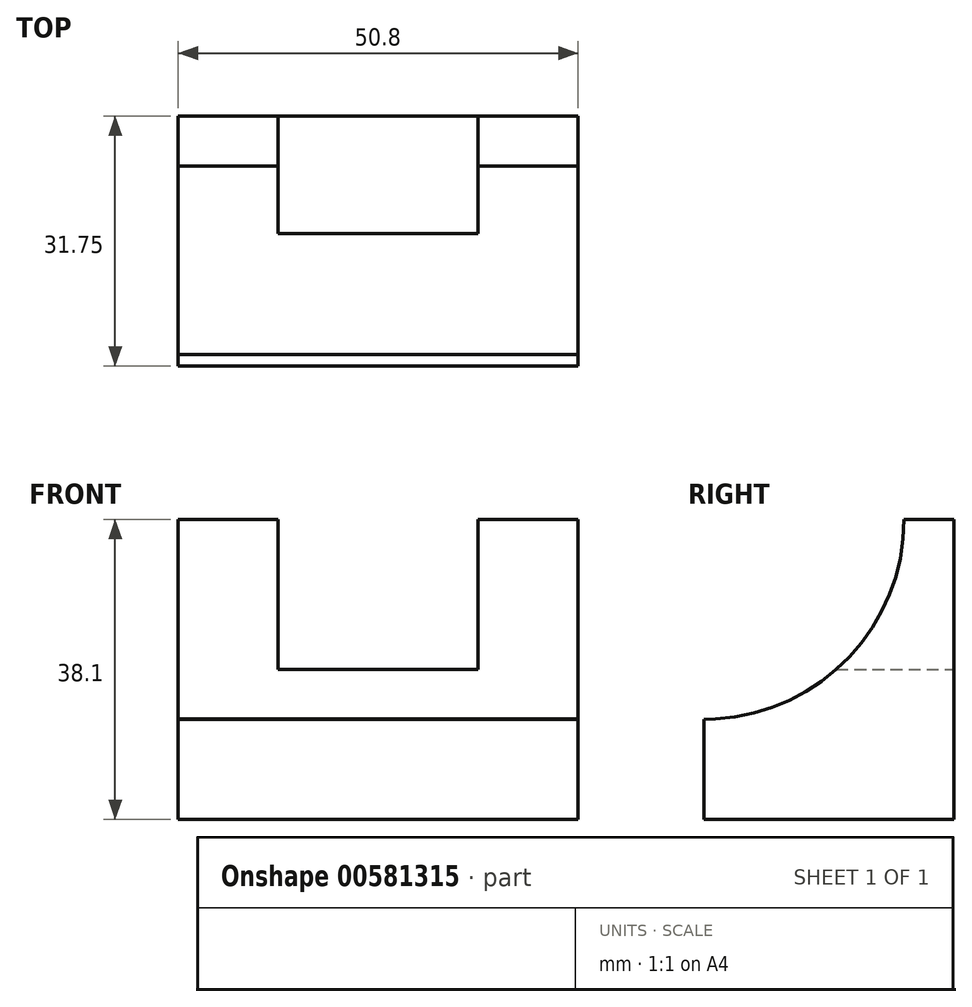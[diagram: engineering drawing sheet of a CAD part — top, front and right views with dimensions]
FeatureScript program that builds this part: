
annotation { "Feature Type Name" : "Feature", "Feature Type Description" : "" }
export const myFeature = defineFeature(function(context is Context, id is Id, definition is map)
    precondition{}
    {
        {
            var Q0;
            Q0=qCreatedBy(makeId("Front.planeOp"),FACE);
            var sketch = newSketch(context, id + "F0", { "sketchPlane" : qUnion([Q0])});
            skLineSegment(sketch, "E0.bottom", {"start": v(-10.98, 24.5) * mm, "end": v(39.82, 24.5) * mm});
            skLineSegment(sketch, "E0.top", {"start": v(-10.98, -13.6) * mm, "end": v(39.82, -13.6) * mm});
            skLineSegment(sketch, "E0.left", {"start": v(-10.98, 24.5) * mm, "end": v(-10.98, -13.6) * mm});
            skLineSegment(sketch, "E0.right", {"start": v(39.82, 24.5) * mm, "end": v(39.82, -13.6) * mm});
            skSolve(sketch);
        }
        {
            var Q0;
            Q0 = qSketchRegion(id + "F0", true);
            extrude(context, id + "F1", {"entities" : qUnion([Q0]), "depth" : 31.75 * mm, "offsetDistance" : 25.4 * mm});
        }
        {
            var Q0;
            Q0=makeQuery(id+"F1.opExtrude","SWEPT_FACE",FACE,{"disambiguationData":[OSD([sQuery(id+"F0.wireOp",EDGE,"E0.right")])]});
            var sketch = newSketch(context, id + "F2", { "sketchPlane" : qUnion([Q0])});
            skArc(sketch, "E1", {"start": v(-31.75, -0.9) * mm, "mid": v(-13.79, 6.53) * mm, "end": v(-6.35, 24.5) * mm});
            skLineSegment(sketch, "E2", {"start": v(-31.75, 24.5) * mm, "end": v(-31.75, -0.9) * mm});
            skLineSegment(sketch, "E3", {"start": v(-31.75, 24.5) * mm, "end": v(-6.35, 24.5) * mm});
            skLineSegment(sketch, "E4", {"start": v(-31.75, -0.9) * mm, "end": v(0, 0) * mm});
            skLineSegment(sketch, "E5", {"start": v(-14.95, -13.6) * mm, "end": v(-14.95, 5.44) * mm});
            skSolve(sketch);
        }
        {
            var Q0;
            {var subQ1=sQuery(id+"F2.wireOp",EDGE,"E2");Q0=makeQuery(id+"F2.imprint","IMPRINT",FACE,{"disambiguationData":[TD([[makeQuery(id+"F2.imprint","IMPRINT",EDGE,{"derivedFrom":subQ1}),1.0]])]});}
            extrude(context, id + "F3", {"entities" : qUnion([Q0]), "operationType" : NewBodyOperationType.REMOVE, "oppositeDirection" : true, "depth" : 254 * mm, "offsetDistance" : 25.4 * mm});
        }
        {
            var Q0;
            Q0=makeQuery(id+"F1.opExtrude","CAP_FACE",FACE,{"disambiguationData":[OSD([sQuery(id+"F0.wireOp",EDGE,"E0.bottom"),sQuery(id+"F0.wireOp",EDGE,"E0.top"),sQuery(id+"F0.wireOp",EDGE,"E0.left"),sQuery(id+"F0.wireOp",EDGE,"E0.right")])],"isStart":true});
            var sketch = newSketch(context, id + "F4", { "sketchPlane" : qUnion([Q0])});
            skLineSegment(sketch, "E6", {"start": v(-39.82, 24.5) * mm, "end": v(-27.12, 24.5) * mm});
            skLineSegment(sketch, "E7", {"start": v(-27.12, 24.5) * mm, "end": v(-27.12, 5.44) * mm});
            skLineSegment(sketch, "E8", {"start": v(-27.12, 5.44) * mm, "end": v(-1.72, 5.44) * mm});
            skLineSegment(sketch, "E9", {"start": v(-1.72, 5.44) * mm, "end": v(-1.72, 24.5) * mm});
            skLineSegment(sketch, "E10", {"start": v(-1.72, 24.5) * mm, "end": v(10.98, 24.5) * mm});
            skSolve(sketch);
        }
        {
            var Q0;
            {var subQ0=sQuery(id+"F4.wireOp",EDGE,"E7");Q0=makeQuery(id+"F4.imprint","IMPRINT",FACE,{"disambiguationData":[TD([[makeQuery(id+"F4.imprint","IMPRINT",EDGE,{"derivedFrom":subQ0}),1.0]])]});}
            extrude(context, id + "F5", {"entities" : qUnion([Q0]), "operationType" : NewBodyOperationType.REMOVE, "oppositeDirection" : true, "depth" : 25.4 * mm, "offsetDistance" : 25.4 * mm});
        }
    });
